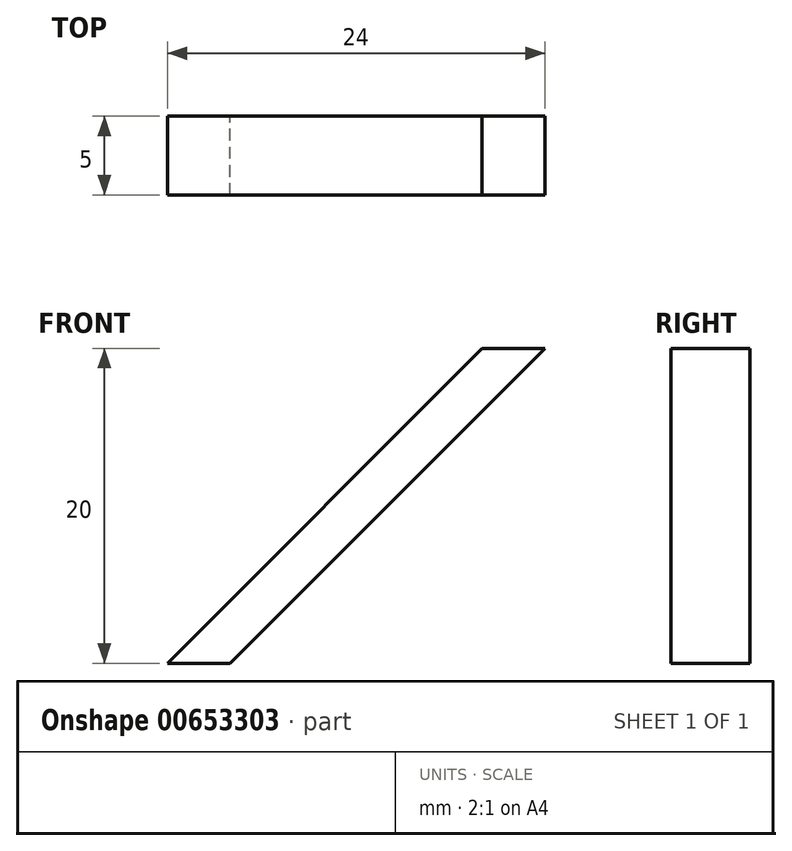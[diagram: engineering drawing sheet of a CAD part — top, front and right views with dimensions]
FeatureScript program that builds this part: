
annotation { "Feature Type Name" : "Feature", "Feature Type Description" : "" }
export const myFeature = defineFeature(function(context is Context, id is Id, definition is map)
    precondition{}
    {
        {
            var Q0;
            Q0=qCreatedBy(makeId("Front.planeOp"),FACE);
            var sketch = newSketch(context, id + "F0", { "sketchPlane" : qUnion([Q0])});
            skLineSegment(sketch, "E0", {"start": v(0, 0) * mm, "end": v(20, 0) * mm});
            skLineSegment(sketch, "E1", {"start": v(20, 0) * mm, "end": v(40, 0) * mm});
            skLineSegment(sketch, "E2", {"start": v(40, 0) * mm, "end": v(40, 20) * mm});
            skLineSegment(sketch, "E3", {"start": v(40, 20) * mm, "end": v(20, 20) * mm});
            skLineSegment(sketch, "E4", {"start": v(20, 20) * mm, "end": v(0, 0) * mm});
            skLineSegment(sketch, "E5", {"start": v(20, 0) * mm, "end": v(40, 20) * mm});
            skLineSegment(sketch, "E6", {"start": v(0, 0) * mm, "end": v(4, 0) * mm});
            skLineSegment(sketch, "E7", {"start": v(4, 0) * mm, "end": v(24, 20) * mm});
            skSolve(sketch);
        }
        {
            var Q0;
            {var subQ0=sQuery(id+"F0.wireOp",EDGE,"E4");Q0=makeQuery(id+"F0.imprint","IMPRINT",FACE,{"disambiguationData":[TD([[makeQuery(id+"F0.imprint","IMPRINT",EDGE,{"derivedFrom":subQ0}),1.0]])]});}
            extrude(context, id + "F1", {"entities" : qUnion([Q0]), "depth" : 5 * mm, "offsetDistance" : 25 * mm});
        }
    });
